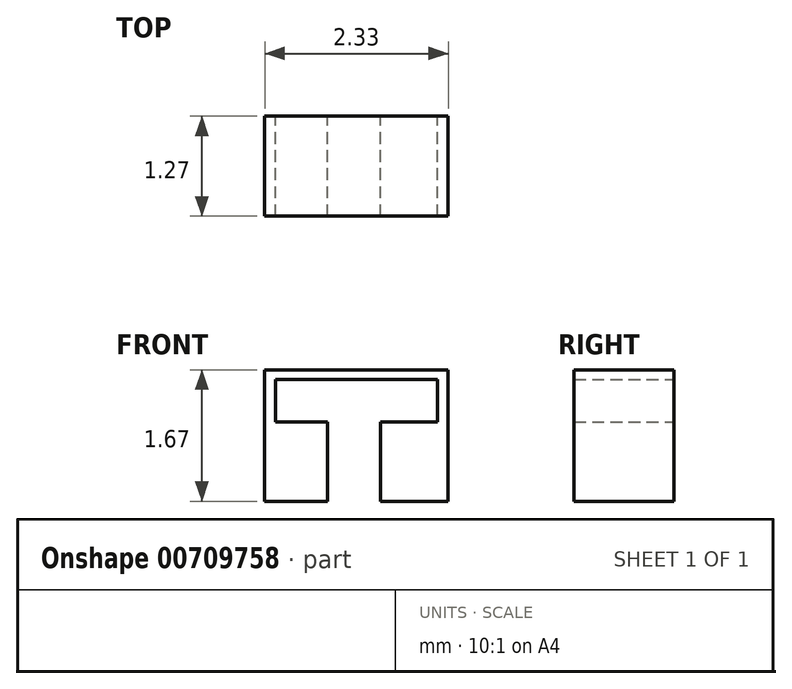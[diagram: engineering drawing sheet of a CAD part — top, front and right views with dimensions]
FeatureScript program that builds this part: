
annotation { "Feature Type Name" : "Feature", "Feature Type Description" : "" }
export const myFeature = defineFeature(function(context is Context, id is Id, definition is map)
    precondition{}
    {
        {
            var Q0;
            Q0=qCreatedBy(makeId("Front.planeOp"),FACE);
            var sketch = newSketch(context, id + "F0", { "sketchPlane" : qUnion([Q0])});
            skLineSegment(sketch, "E0", {"start": v(0.93, -0.38) * mm, "end": v(0.93, 0.62) * mm});
            skLineSegment(sketch, "E1", {"start": v(0.27, 0.62) * mm, "end": v(0.27, 1.17) * mm});
            skLineSegment(sketch, "E2", {"start": v(0.27, 1.17) * mm, "end": v(2.33, 1.17) * mm});
            skLineSegment(sketch, "E3", {"start": v(2.33, 1.17) * mm, "end": v(2.33, 0.62) * mm});
            skLineSegment(sketch, "E4", {"start": v(1.6, 0.62) * mm, "end": v(1.6, -0.38) * mm});
            skLineSegment(sketch, "E5", {"start": v(0.13, 0.62) * mm, "end": v(0.13, 1.29) * mm});
            skLineSegment(sketch, "E6", {"start": v(0.13, 1.29) * mm, "end": v(2.46, 1.29) * mm});
            skLineSegment(sketch, "E7", {"start": v(2.46, 1.29) * mm, "end": v(2.46, 0.62) * mm});
            skLineSegment(sketch, "E8", {"start": v(2.46, 0.62) * mm, "end": v(2.46, -0.38) * mm});
            skLineSegment(sketch, "E9", {"start": v(2.46, -0.38) * mm, "end": v(1.6, -0.38) * mm});
            skLineSegment(sketch, "E10", {"start": v(1.6, 0.62) * mm, "end": v(2.33, 0.62) * mm});
            skLineSegment(sketch, "E11", {"start": v(0.93, -0.38) * mm, "end": v(0.13, -0.38) * mm});
            skLineSegment(sketch, "E12", {"start": v(0.13, -0.38) * mm, "end": v(0.13, 0.62) * mm});
            skLineSegment(sketch, "E13", {"start": v(0.27, 0.62) * mm, "end": v(0.93, 0.62) * mm});
            skSolve(sketch);
        }
        {
            var Q0;
            Q0=makeQuery(id+"F0.imprint","IMPRINT",FACE,{"disambiguationData":[TD([[makeQuery(id+"F0.imprint","IMPRINT",EDGE,{"derivedFrom":sQuery(id+"F0.wireOp",EDGE,"E0")}),1.0]])]});
            extrude(context, id + "F1", {"entities" : qUnion([Q0]), "depth" : 1.27 * mm, "offsetDistance" : 25.4 * mm});
        }
    });
